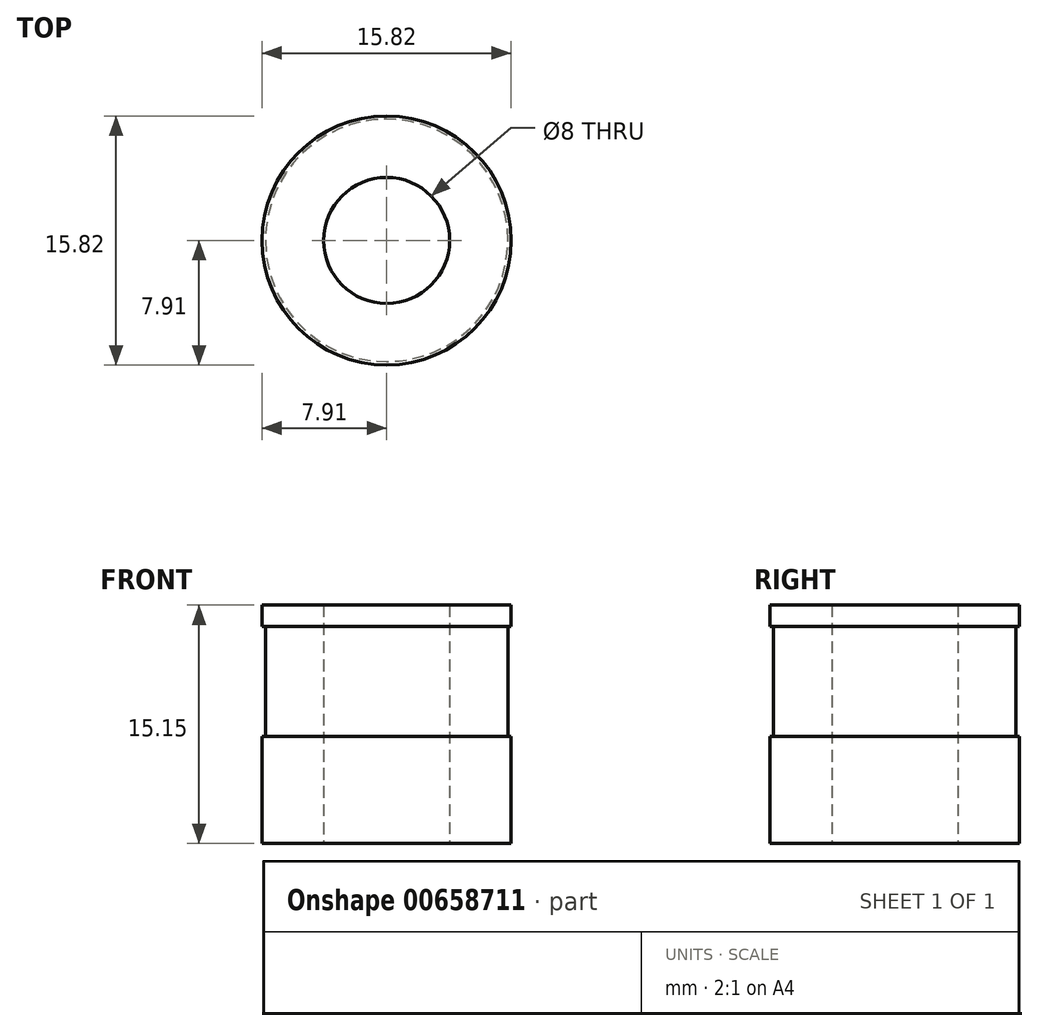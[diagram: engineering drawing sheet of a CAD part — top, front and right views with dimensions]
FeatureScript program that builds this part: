
annotation { "Feature Type Name" : "Feature", "Feature Type Description" : "" }
export const myFeature = defineFeature(function(context is Context, id is Id, definition is map)
    precondition{}
    {
        {
            var Q0;
            Q0=qCreatedBy(makeId("Front.planeOp"),FACE);
            var sketch = newSketch(context, id + "F0", { "sketchPlane" : qUnion([Q0])});
            skLineSegment(sketch, "E0", {"start": v(4, 15.15) * mm, "end": v(4, 0) * mm});
            skLineSegment(sketch, "E1", {"start": v(4, 0) * mm, "end": v(7.9, 0) * mm});
            skLineSegment(sketch, "E2", {"start": v(7.9, 0) * mm, "end": v(7.9, 6.8) * mm});
            skLineSegment(sketch, "E3", {"start": v(7.9, 6.8) * mm, "end": v(7.7, 6.8) * mm});
            skLineSegment(sketch, "E4", {"start": v(7.7, 6.8) * mm, "end": v(7.7, 13.8) * mm});
            skLineSegment(sketch, "E5", {"start": v(7.7, 13.8) * mm, "end": v(7.9, 13.8) * mm});
            skLineSegment(sketch, "E6", {"start": v(7.9, 13.8) * mm, "end": v(7.9, 15.15) * mm});
            skLineSegment(sketch, "E7", {"start": v(7.9, 15.15) * mm, "end": v(4, 15.15) * mm});
            skLineSegment(sketch, "E8", {"start": v(0, 0) * mm, "end": v(0, 11.59) * mm});
            skSolve(sketch);
        }
        {
            var Q0;
            Q0=makeQuery(id+"F0.imprint","IMPRINT",FACE,{"disambiguationData":[TD([[makeQuery(id+"F0.imprint","IMPRINT",EDGE,{"derivedFrom":sQuery(id+"F0.wireOp",EDGE,"E0")}),1.0]])]});
            var Q1;
            Q1=sQuery(id+"F0.wireOp",EDGE,"E8");
            revolve(context, id + "F1", {"entities" : qUnion([Q0]), "axis" : qUnion([Q1]), "revolveType" : RevolveType.FULL});
        }
    });
